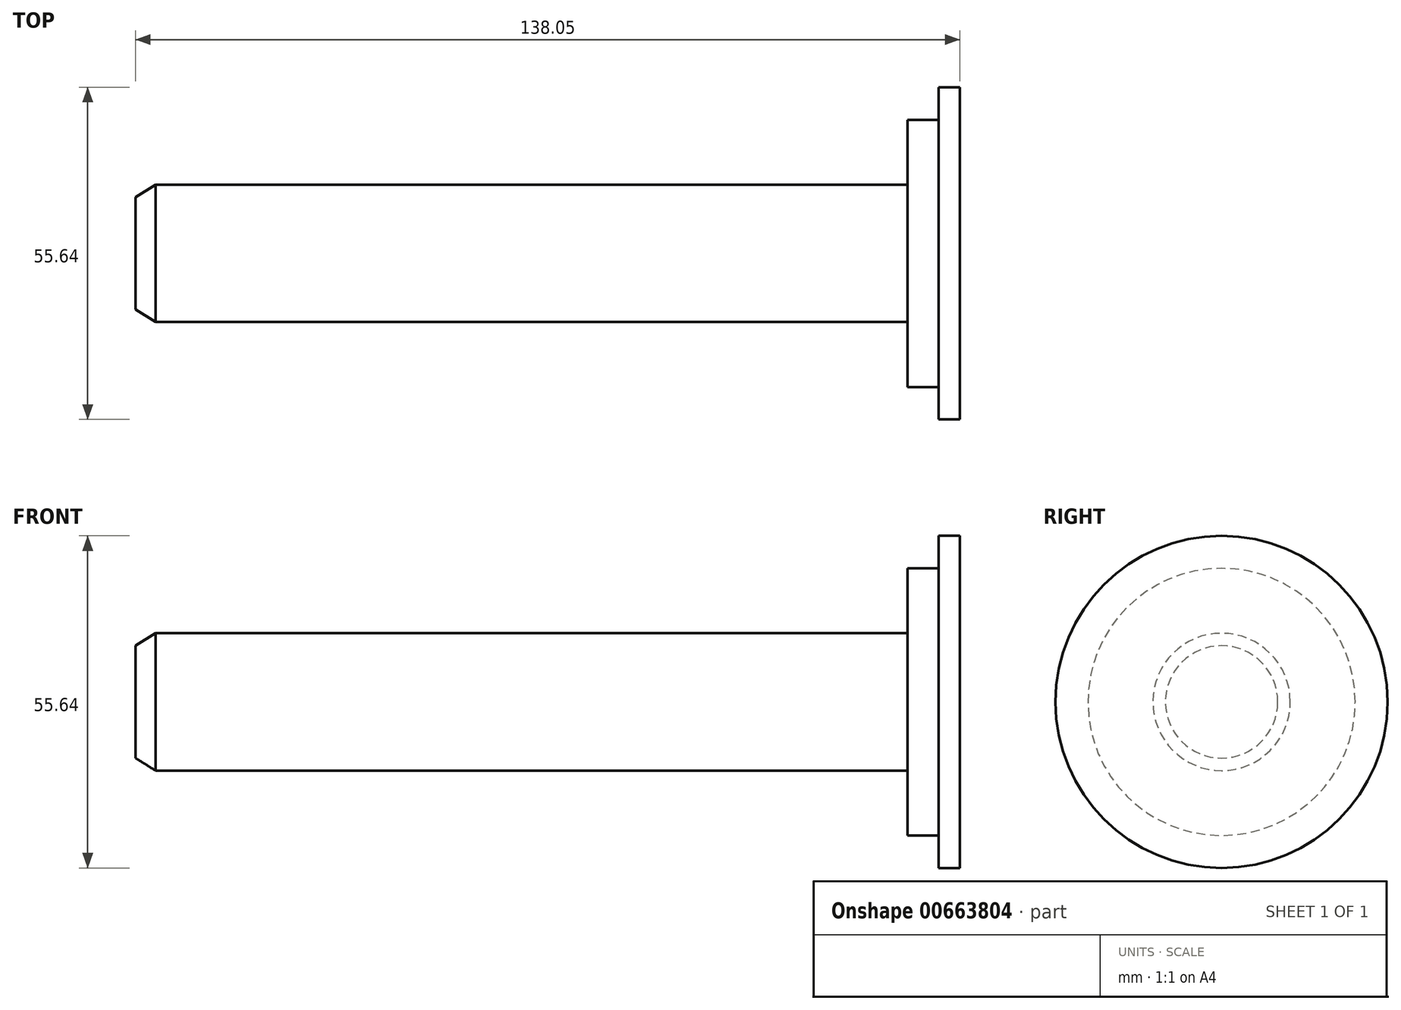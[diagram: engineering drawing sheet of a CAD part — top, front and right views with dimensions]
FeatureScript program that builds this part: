
annotation { "Feature Type Name" : "Feature", "Feature Type Description" : "" }
export const myFeature = defineFeature(function(context is Context, id is Id, definition is map)
    precondition{}
    {
        {
            var Q0;
            Q0=qCreatedBy(makeId("Front.planeOp"),FACE);
            var sketch = newSketch(context, id + "F0", { "sketchPlane" : qUnion([Q0])});
            skLineSegment(sketch, "E0", {"start": v(-111.8, 0) * mm, "end": v(-111.8, -9.41) * mm});
            skLineSegment(sketch, "E1", {"start": v(-111.8, -9.41) * mm, "end": v(-108.46, -11.5) * mm});
            skLineSegment(sketch, "E2", {"start": v(-108.46, -11.5) * mm, "end": v(17.47, -11.5) * mm});
            skLineSegment(sketch, "E3", {"start": v(17.47, -11.5) * mm, "end": v(17.47, -22.38) * mm});
            skLineSegment(sketch, "E4", {"start": v(17.47, -22.38) * mm, "end": v(22.7, -22.38) * mm});
            skLineSegment(sketch, "E5", {"start": v(22.7, -22.38) * mm, "end": v(22.7, -27.82) * mm});
            skLineSegment(sketch, "E6", {"start": v(22.7, -27.82) * mm, "end": v(26.25, -27.82) * mm});
            skLineSegment(sketch, "E7", {"start": v(26.25, -27.82) * mm, "end": v(26.25, 0) * mm});
            skLineSegment(sketch, "E8", {"start": v(26.25, 0) * mm, "end": v(-111.8, 0) * mm});
            skSolve(sketch);
        }
        {
            var Q0;
            Q0 = qSketchRegion(id + "F0", true);
            var Q1;
            Q1=sQuery(id+"F0.wireOp",EDGE,"E8");
            revolve(context, id + "F1", {"entities" : qUnion([Q0]), "axis" : qUnion([Q1]), "revolveType" : RevolveType.FULL});
        }
    });
